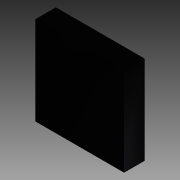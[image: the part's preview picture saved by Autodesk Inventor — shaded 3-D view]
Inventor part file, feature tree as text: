
AUTODESK INVENTOR PART (.ipt)
format: ipt  version: 2014 (Build 180170000, 170)  size: 168,960 bytes
history: native  units: in
note: dims shown in document units (in); Inventor stores cm internally (conversion verified against a paired STEP export)
features: extrude x3, sketch x3, plane x1, pattern_linear x1, pattern_circular x1, projected_geometry x1
ambient origin geometry x8: Origin, YZ Plane, XZ Plane, XY Plane, X Axis, Y Axis, Z Axis, Center Point
bodies: Solid1 (feature_tree)
feature tree (10):
  extrude  "Extrusion1"  Depth=0.1575in
  plane  "Work Plane1"
  extrude  "Extrusion2"  Depth=0.0031in
  pattern_linear  "Rectangular Pattern1"  Spacing1=0.0118in  [1 undecoded]
  pattern_circular  "Circular Pattern1"  Count=4  [1 undecoded]
  extrude  "Extrusion3"  Depth=0.08in
  sketch  "Sketch1"  dims[d0=0.1575in d1=0.1575in]
  sketch  "Sketch2"  dims[d2=0.0362in d3=0.0in d4=0.0031in]
  projected_geometry  "Projected Loop1"
  sketch  "Sketch3"  dims[d7=0.0151in d8=0.0118in d9=1.5748in d11=0.0256in d12=0.3937in d14=1.0in d16=0.0128in d17=0.0079in d18=0.0in d19=1.5748in d21=0.0256in d22=0.0787in d23=0.0787in d24=1.5748in d25=360.0deg d27=0.08in d28=0.08in d29=0.04in d30=0.04in d31=0.0079in d32=0.0in]
note: 2 required parameter values undecoded (feature->parameter linkage not recoverable at this tier; creation-order binding heuristic only, values carry confidence <= 0.55)
